# Revit family: Hand_Dryer-World_Dryer-SLIMdri
name_source: partatom
category: Specialty Equipment
revit_build: Autodesk Revit Architecture 2015 (Build: 20140606_1530(x64)
units: mm (PartAtom-declared; Revit-internal decimal feet)

## types (2) — shared parameters
Apparent Load = 950 VA
CFM = 70 CFM
Depth = 0' - 3 15/16"
Description = Surface Mounted ADA Compliant Hand Dryer
Height = 0' - 10 11/16"
Manufacturer = World Dryer
Motor Speed (RPM) = 13000
Number of Poles = 1
Outside Casing = Metal - World Dryer - Aluminum - White
Phase = 1
Power Factor = 1
Product Documentation Link = http://www.worlddryer.com
Product Name = SLIMdri
Product Page URL = http://worlddryer.com
Product data url = https://bimobject.com
Sell Sheet = http://www.worlddryer.com
URL = http://worlddryer.com
Unit Casing = Metal - World Dryer - Aluminum - Black
Voltage = 240 V
Wattage = 950 W
Width = 0' - 11 7/16"

## per-type parameters (varying)
| type | Frequency | Model |
| Model L-Universal Voltage | 60 Hz | Model L - Universal Voltage |
| Model L48 | 50 Hz | Model L48 |

## geometry (parser evidence)
native form markers: Blend x20, Sweep x8
no freeform markers — native parametric forms only
